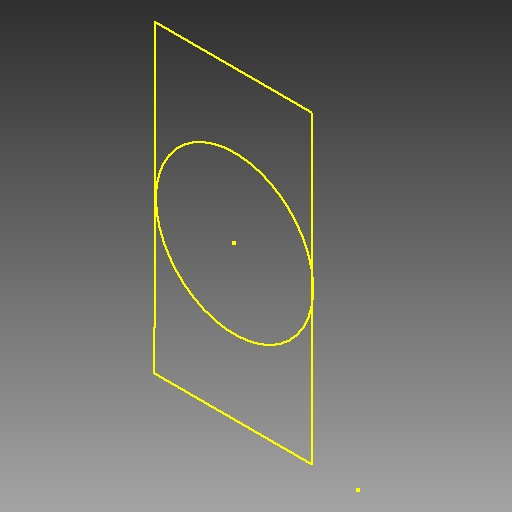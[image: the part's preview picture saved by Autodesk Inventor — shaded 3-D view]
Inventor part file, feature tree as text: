
AUTODESK INVENTOR PART (.ipt)
format: ipt  version: 2018 (Build 220112000, 112)  size: 71,168 bytes
history: native  units: mm
features: other x1, sketch x1
ambient origin geometry x8: Origin, YZ Plane, XZ Plane, XY Plane, X Axis, Y Axis, Z Axis, Center Point
feature tree (2):
  other  "Working Axis etc.ipt"
  sketch  "Sketch1"  dims[d0=10.0mm]
